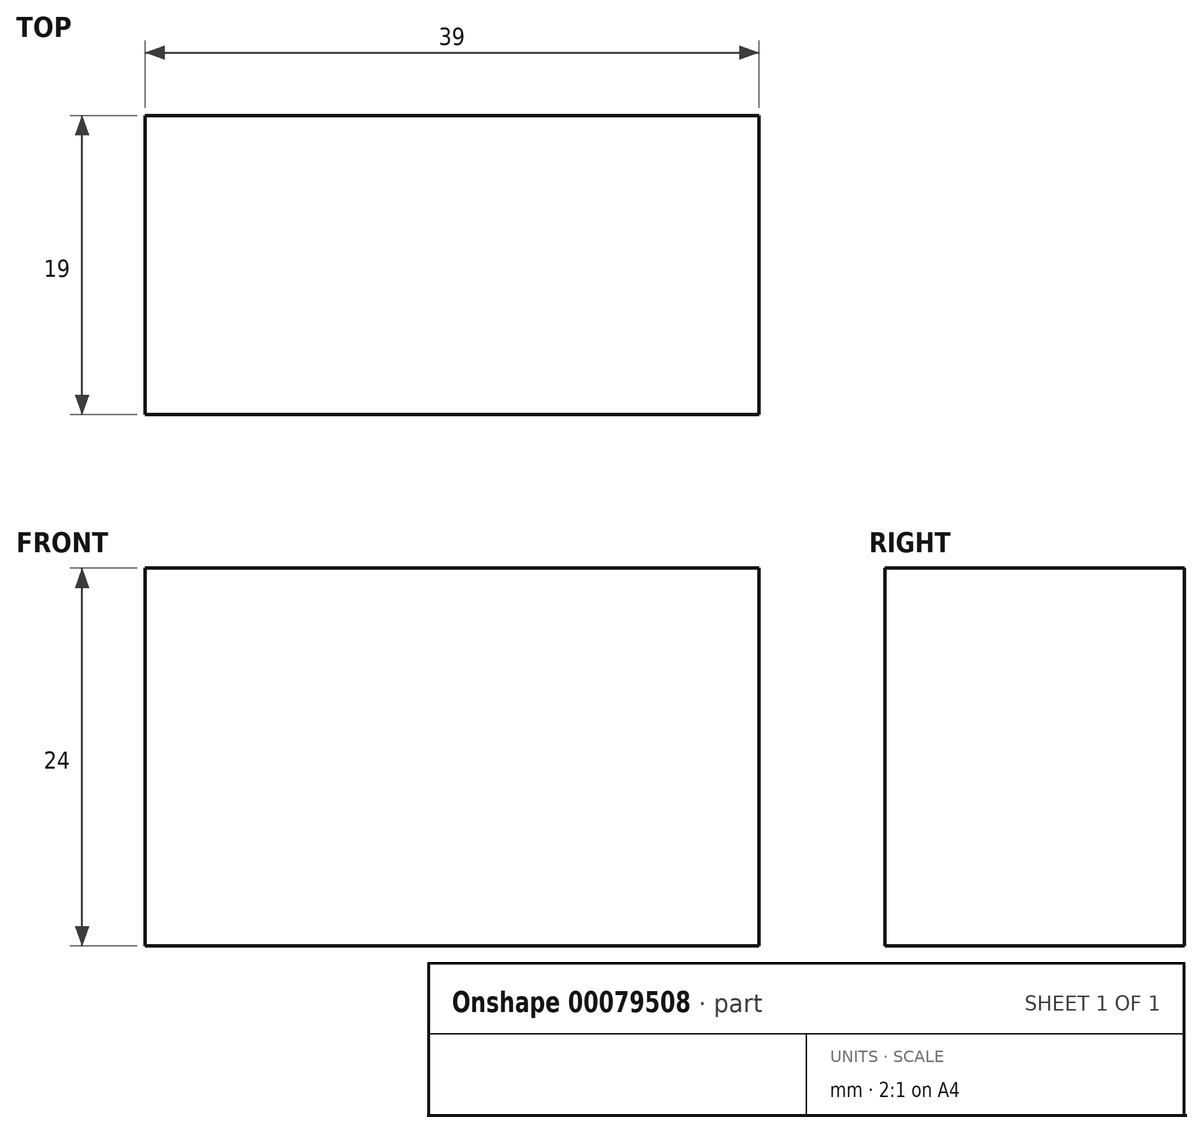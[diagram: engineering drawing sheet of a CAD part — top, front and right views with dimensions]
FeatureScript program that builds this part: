
annotation { "Feature Type Name" : "Feature", "Feature Type Description" : "" }
export const myFeature = defineFeature(function(context is Context, id is Id, definition is map)
    precondition{}
    {
        {
            var Q0;
            Q0=qCreatedBy(makeId("Right.planeOp"),FACE);
            var sketch = newSketch(context, id + "F0", { "sketchPlane" : qUnion([Q0])});
            skLineSegment(sketch, "E0.bottom", {"start": v(-9.5, 24) * mm, "end": v(9.5, 24) * mm});
            skLineSegment(sketch, "E0.top", {"start": v(-9.5, 0) * mm, "end": v(9.5, 0) * mm});
            skLineSegment(sketch, "E0.left", {"start": v(-9.5, 24) * mm, "end": v(-9.5, 0) * mm});
            skLineSegment(sketch, "E0.right", {"start": v(9.5, 24) * mm, "end": v(9.5, 0) * mm});
            skSolve(sketch);
        }
        {
            var Q0;
            Q0 = qSketchRegion(id + "F0", true);
            extrude(context, id + "F1", {"entities" : qUnion([Q0]), "depth" : 39 * mm, "symmetric" : true});
        }
    });
